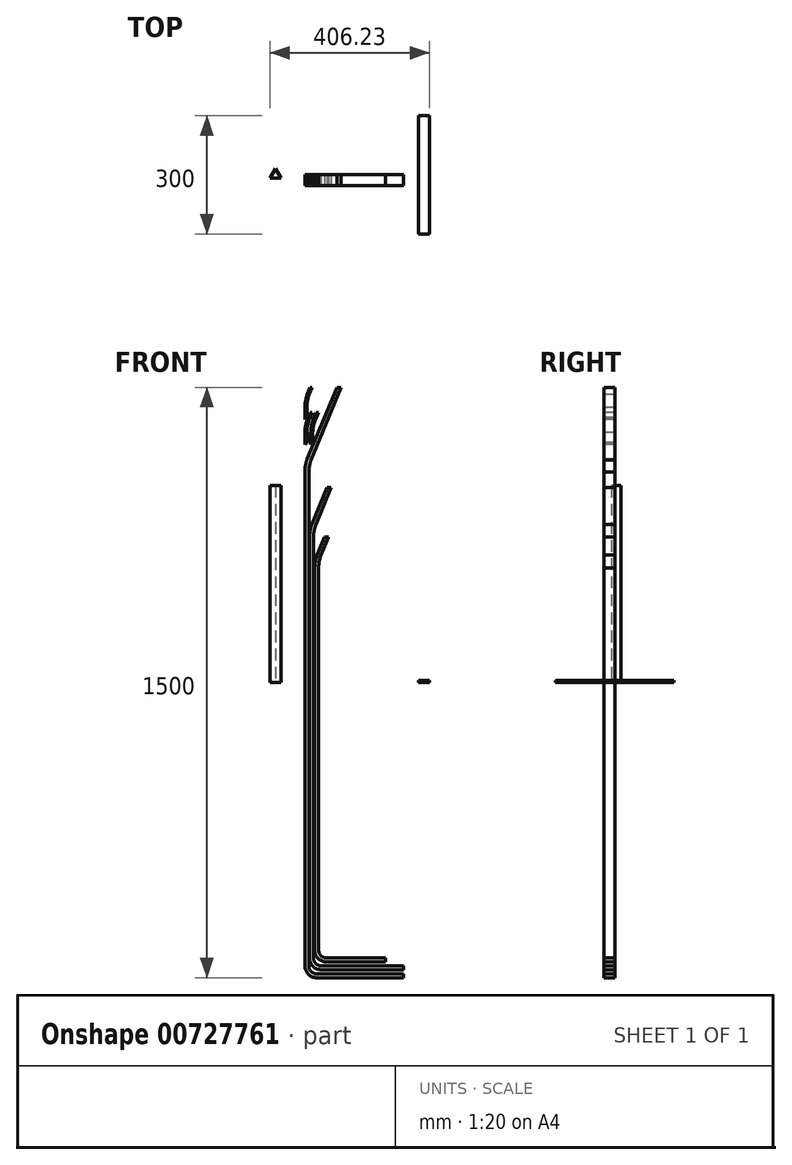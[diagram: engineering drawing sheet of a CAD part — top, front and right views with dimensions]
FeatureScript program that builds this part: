
annotation { "Feature Type Name" : "Feature", "Feature Type Description" : "" }
export const myFeature = defineFeature(function(context is Context, id is Id, definition is map)
    precondition{}
    {
        {
            var Q0;
            Q0=qCreatedBy(makeId("Front.planeOp"),FACE);
            var sketch = newSketch(context, id + "F0", { "sketchPlane" : qUnion([Q0])});
            skLineSegment(sketch, "E0.bottom", {"start": v(-125, -750) * mm, "end": v(125, -750) * mm});
            skLineSegment(sketch, "E0.top", {"start": v(-125, 750) * mm, "end": v(125, 750) * mm});
            skLineSegment(sketch, "E0.left", {"start": v(-125, -750) * mm, "end": v(-125, 750) * mm});
            skLineSegment(sketch, "E0.right", {"start": v(125, -750) * mm, "end": v(125, 750) * mm});
            skPoint(sketch, "E0.middle", {"position": v(0, 0) * mm});
            skSolve(sketch);
        }
        {
            var Q0;
            Q0 = qSketchRegion(id + "F0", true);
            extrude(context, id + "F1", {"entities" : qUnion([Q0]), "flatOperationType" : FlatOperationType.REMOVE, "depth" : 28 * mm, "offsetDistance" : 25 * mm, "domain" : OperationDomain.MODEL});
        }
        {
            var Q0;
            Q0=makeQuery(id+"F1.opExtrude","CAP_FACE",FACE,{"disambiguationData":[OSD([sQuery(id+"F0.wireOp",EDGE,"E0.bottom"),sQuery(id+"F0.wireOp",EDGE,"E0.top"),sQuery(id+"F0.wireOp",EDGE,"E0.left"),sQuery(id+"F0.wireOp",EDGE,"E0.right")])],"isStart":false});
            var sketch = newSketch(context, id + "F2", { "sketchPlane" : qUnion([Q0])});
            skArc(sketch, "E1", {"start": v(-115, -720) * mm, "mid": v(-109.14, -734.14) * mm, "end": v(-95, -740) * mm});
            skLineSegment(sketch, "E2", {"start": v(-95, -740) * mm, "end": v(125, -740) * mm});
            skArc(sketch, "E3", {"start": v(-125, -720) * mm, "mid": v(-116.21, -741.21) * mm, "end": v(-95, -750) * mm});
            skLineSegment(sketch, "E4", {"start": v(-95, -750) * mm, "end": v(125, -750) * mm});
            skArc(sketch, "E5", {"start": v(-109, 566.01) * mm, "mid": v(-113.23, 550.74) * mm, "end": v(-115, 535) * mm});
            skLineSegment(sketch, "E6", {"start": v(-115, 535) * mm, "end": v(-115, -720) * mm});
            skLineSegment(sketch, "E7", {"start": v(-109, 566.01) * mm, "end": v(-32.79, 750) * mm});
            skArc(sketch, "E8", {"start": v(-119, 568) * mm, "mid": v(-123.27, 551.73) * mm, "end": v(-125, 535) * mm});
            skLineSegment(sketch, "E9", {"start": v(-125, 535) * mm, "end": v(-125, -720) * mm});
            skLineSegment(sketch, "E10", {"start": v(-119, 568) * mm, "end": v(-43.61, 750) * mm});
            skLineSegment(sketch, "E11", {"start": v(125, -730) * mm, "end": v(-83.22, -730) * mm});
            skArc(sketch, "E12", {"start": v(-113.22, -700) * mm, "mid": v(-104.43, -721.21) * mm, "end": v(-83.22, -730) * mm});
            skLineSegment(sketch, "E13", {"start": v(-113.22, -700) * mm, "end": v(-113.22, 370) * mm});
            skArc(sketch, "E14", {"start": v(-107.22, 403) * mm, "mid": v(-111.48, 386.73) * mm, "end": v(-113.22, 370) * mm});
            skLineSegment(sketch, "E15", {"start": v(-107.22, 403) * mm, "end": v(-68.95, 495.39) * mm});
            skLineSegment(sketch, "E16", {"start": v(-68.95, 495.39) * mm, "end": v(-58.12, 495.39) * mm});
            skLineSegment(sketch, "E17", {"start": v(-58.12, 495.39) * mm, "end": v(-97.22, 401.01) * mm});
            skArc(sketch, "E18", {"start": v(-97.22, 401.01) * mm, "mid": v(-101.45, 385.74) * mm, "end": v(-103.22, 370) * mm});
            skLineSegment(sketch, "E19", {"start": v(-103.22, 370) * mm, "end": v(-103.22, -700) * mm});
            skArc(sketch, "E20", {"start": v(-103.22, -700) * mm, "mid": v(-97.36, -714.14) * mm, "end": v(-83.22, -720) * mm});
            skLineSegment(sketch, "E21", {"start": v(-83.22, -720) * mm, "end": v(125, -720) * mm});
            skLineSegment(sketch, "E22", {"start": v(-70, -710) * mm, "end": v(80, -710) * mm});
            skLineSegment(sketch, "E23", {"start": v(80, -710) * mm, "end": v(80, -700) * mm});
            skLineSegment(sketch, "E24", {"start": v(80, -700) * mm, "end": v(-70, -700) * mm});
            skArc(sketch, "E25", {"start": v(-100, -680) * mm, "mid": v(-91.21, -701.21) * mm, "end": v(-70, -710) * mm});
            skArc(sketch, "E26", {"start": v(-90, -680) * mm, "mid": v(-84.14, -694.14) * mm, "end": v(-70, -700) * mm});
            skLineSegment(sketch, "E27", {"start": v(-100, -680) * mm, "end": v(-100, 290.8) * mm});
            skLineSegment(sketch, "E28", {"start": v(-90, -680) * mm, "end": v(-90, 290.8) * mm});
            skArc(sketch, "E29", {"start": v(-94, 323.8) * mm, "mid": v(-98.27, 307.54) * mm, "end": v(-100, 290.8) * mm});
            skArc(sketch, "E30", {"start": v(-84, 323.8) * mm, "mid": v(-88.4, 307.56) * mm, "end": v(-90, 290.8) * mm});
            skLineSegment(sketch, "E31", {"start": v(-94, 323.8) * mm, "end": v(-74.87, 370) * mm});
            skLineSegment(sketch, "E32", {"start": v(-84, 323.8) * mm, "end": v(-64.87, 370) * mm});
            skLineSegment(sketch, "E33", {"start": v(-64.87, 370) * mm, "end": v(-74.87, 370) * mm});
            skLineSegment(sketch, "E34", {"start": v(-111.35, 750) * mm, "end": v(-119, 731.52) * mm});
            skArc(sketch, "E35", {"start": v(-119, 731.52) * mm, "mid": v(-123.27, 715.25) * mm, "end": v(-125, 698.52) * mm});
            skLineSegment(sketch, "E36", {"start": v(-120, 698.52) * mm, "end": v(-120, 673.52) * mm});
            skLineSegment(sketch, "E37", {"start": v(-125, 668.52) * mm, "end": v(-120, 673.52) * mm});
            skArc(sketch, "E38", {"start": v(-114, 731.52) * mm, "mid": v(-118.4, 715.28) * mm, "end": v(-120, 698.52) * mm});
            skLineSegment(sketch, "E39", {"start": v(-114, 731.52) * mm, "end": v(-106.35, 750) * mm});
            skLineSegment(sketch, "E40", {"start": v(-111.35, 686.36) * mm, "end": v(-119, 667.88) * mm});
            skArc(sketch, "E41", {"start": v(-119, 667.88) * mm, "mid": v(-123.27, 651.61) * mm, "end": v(-125, 634.88) * mm});
            skLineSegment(sketch, "E42", {"start": v(-120, 634.88) * mm, "end": v(-120, 609.88) * mm});
            skLineSegment(sketch, "E43", {"start": v(-125, 604.88) * mm, "end": v(-120, 609.88) * mm});
            skArc(sketch, "E44", {"start": v(-114, 667.88) * mm, "mid": v(-118.4, 651.64) * mm, "end": v(-120, 634.88) * mm});
            skLineSegment(sketch, "E45", {"start": v(-114, 667.88) * mm, "end": v(-106.35, 686.36) * mm});
            skLineSegment(sketch, "E46", {"start": v(-106.35, 686.36) * mm, "end": v(-111.35, 686.36) * mm});
            skLineSegment(sketch, "E47", {"start": v(-111.35, 750) * mm, "end": v(-125, 750) * mm});
            skLineSegment(sketch, "E48", {"start": v(-125, 750) * mm, "end": v(-125, 698.52) * mm});
            skLineSegment(sketch, "E49", {"start": v(-106.35, 750) * mm, "end": v(-43.61, 750) * mm});
            skLineSegment(sketch, "E50", {"start": v(-32.79, 750) * mm, "end": v(125, 750) * mm});
            skLineSegment(sketch, "E51", {"start": v(125, 750) * mm, "end": v(125, -720) * mm});
            skLineSegment(sketch, "E52", {"start": v(125, -730) * mm, "end": v(125, -740) * mm});
            skLineSegment(sketch, "E53", {"start": v(-125, -720) * mm, "end": v(-125, -750) * mm});
            skLineSegment(sketch, "E54", {"start": v(-125, -750) * mm, "end": v(-95, -750) * mm});
            skLineSegment(sketch, "E55", {"start": v(-125, 604.88) * mm, "end": v(-125, 535) * mm});
            skLineSegment(sketch, "E56", {"start": v(-125, 668.52) * mm, "end": v(-125, 634.88) * mm});
            skLineSegment(sketch, "E57", {"start": v(-110, 604.88) * mm, "end": v(-110, 634.88) * mm});
            skLineSegment(sketch, "E58", {"start": v(-110, 604.88) * mm, "end": v(-105, 609.88) * mm});
            skLineSegment(sketch, "E59", {"start": v(-105, 609.88) * mm, "end": v(-105, 634.88) * mm});
            skLineSegment(sketch, "E60", {"start": v(-104, 667.88) * mm, "end": v(-96.35, 686.36) * mm});
            skPoint(sketch, "E60.endSnap0", {"position": v(-108.85, 686.36) * mm});
            skLineSegment(sketch, "E61", {"start": v(-96.35, 686.36) * mm, "end": v(-90.35, 686.36) * mm});
            skLineSegment(sketch, "E62", {"start": v(-90.35, 686.36) * mm, "end": v(-98, 667.88) * mm});
            skArc(sketch, "E63", {"start": v(-104, 667.88) * mm, "mid": v(-108.27, 651.61) * mm, "end": v(-110, 634.88) * mm});
            skArc(sketch, "E64", {"start": v(-98, 667.88) * mm, "mid": v(-102.9, 651.68) * mm, "end": v(-105, 634.88) * mm});
            skSolve(sketch);
        }
        {
            var Q0;
            Q0 = qSketchRegion(id + "F2", true);
            extrude(context, id + "F3", {"entities" : qUnion([Q0]), "operationType" : NewBodyOperationType.REMOVE, "oppositeDirection" : true, "depth" : 28 * mm, "offsetDistance" : 25 * mm});
        }
        {
            var Q0;
            Q0=qCreatedBy(makeId("Top.planeOp"),FACE);
            var sketch = newSketch(context, id + "F4", { "sketchPlane" : qUnion([Q0])});
            skCircle(sketch, "E65.cCircle", {"center": v(-200, 0) * mm, "radius": 16.17 * mm, "construction": true});
            skLineSegment(sketch, "E65.0", {"start": v(-214, -8.08) * mm, "end": v(-200, 16.17) * mm});
            skLineSegment(sketch, "E65.1", {"start": v(-200, 16.17) * mm, "end": v(-186, -8.08) * mm});
            skLineSegment(sketch, "E65.2", {"start": v(-186, -8.08) * mm, "end": v(-214, -8.08) * mm});
            skSolve(sketch);
        }
        {
            var Q0;
            Q0 = qSketchRegion(id + "F4", true);
            extrude(context, id + "F5", {"entities" : qUnion([Q0]), "depth" : 500 * mm, "offsetDistance" : 25 * mm});
        }
        {
            var Q0;
            Q0=qCreatedBy(makeId("Top.planeOp"), FACE);
            var sketch = newSketch(context, id + "F6", { "sketchPlane" : qUnion([Q0])});
            skLineSegment(sketch, "E66.bottom", {"start": v(192.23, -150) * mm, "end": v(164.23, -150) * mm});
            skLineSegment(sketch, "E66.top", {"start": v(192.23, 150) * mm, "end": v(164.23, 150) * mm});
            skLineSegment(sketch, "E66.left", {"start": v(192.23, -150) * mm, "end": v(192.23, 150) * mm});
            skLineSegment(sketch, "E66.right", {"start": v(164.23, -150) * mm, "end": v(164.23, 150) * mm});
            skPoint(sketch, "E66.middle", {"position": v(178.23, 0) * mm, "construction": true});
            skSolve(sketch);
        }
        {
            var Q0;
            Q0 = qSketchRegion(id + "F6", true);
            extrude(context, id + "F7", {"entities" : qUnion([Q0]), "domain" : OperationDomain.MODEL, "flatOperationType" : FlatOperationType.REMOVE, "depth" : 5 * mm, "offsetDistance" : 25 * mm});
        }
    });
